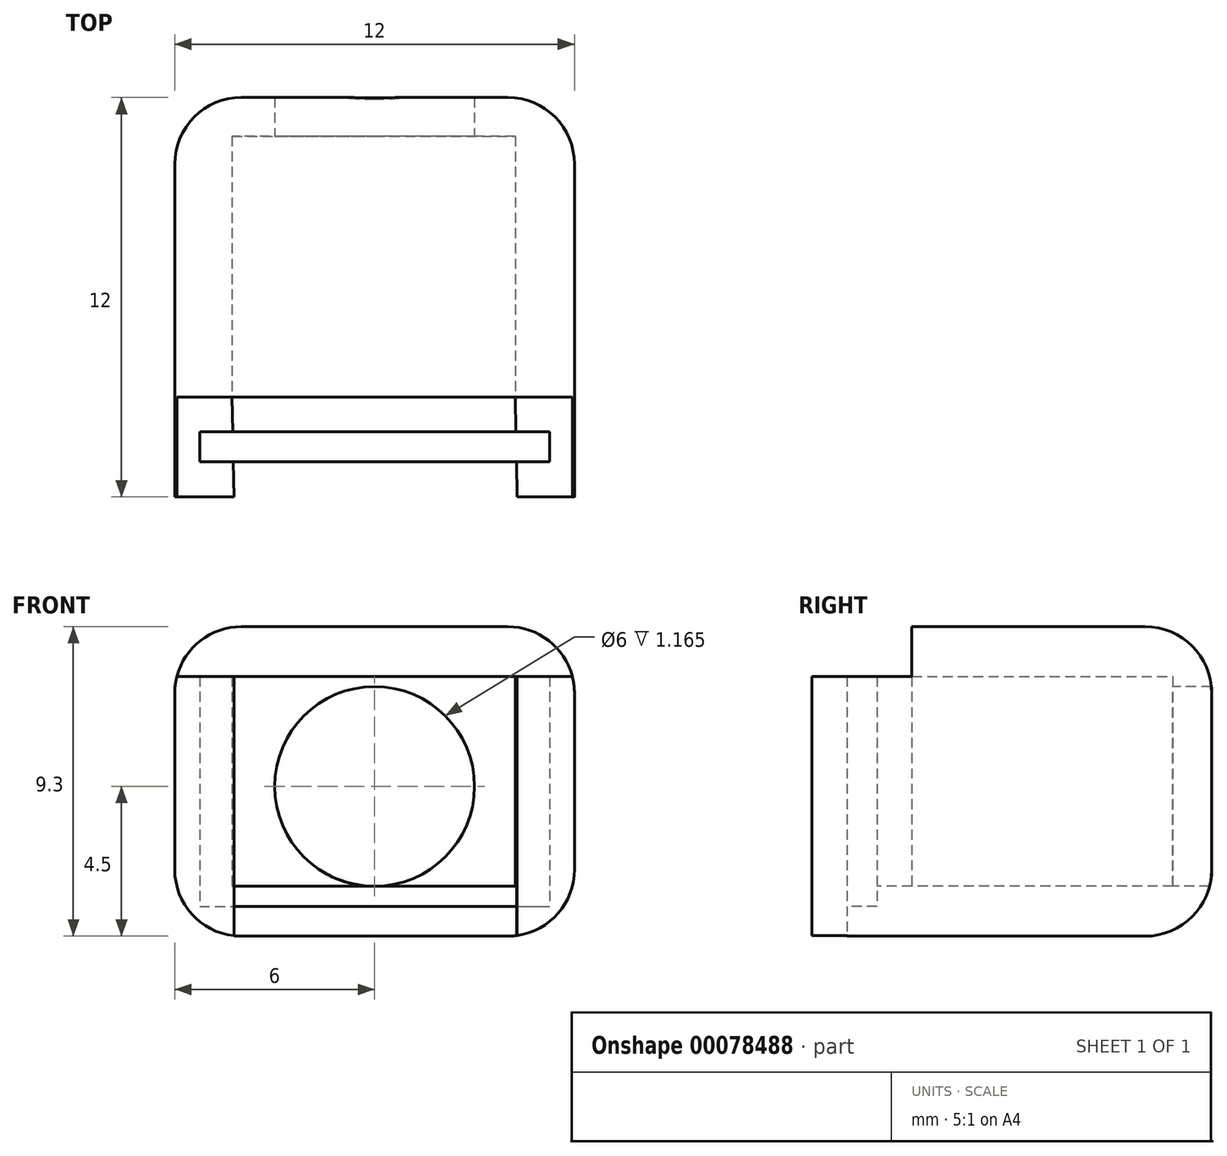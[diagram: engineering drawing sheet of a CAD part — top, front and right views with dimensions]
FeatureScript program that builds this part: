
annotation { "Feature Type Name" : "Feature", "Feature Type Description" : "" }
export const myFeature = defineFeature(function(context is Context, id is Id, definition is map)
    precondition{}
    {
        {
            var Q0;
            Q0=qCreatedBy(makeId("Top.planeOp"),FACE);
            var sketch = newSketch(context, id + "F0", { "sketchPlane" : qUnion([Q0])});
            skPoint(sketch, "E0.rect.middle", {"position": v(0, 0) * mm});
            skLineSegment(sketch, "E1.rect.bottom", {"start": v(-6, -1.5) * mm, "end": v(6, -1.5) * mm});
            skLineSegment(sketch, "E1.rect.top", {"start": v(-6, 1.5) * mm, "end": v(-4.28, 1.5) * mm});
            skLineSegment(sketch, "E1.rect.left", {"start": v(-6, -1.5) * mm, "end": v(-6, 1.5) * mm});
            skLineSegment(sketch, "E1.rect.right", {"start": v(6, -1.5) * mm, "end": v(6, 1.5) * mm});
            skLineSegment(sketch, "E2.rect.bottom", {"start": v(5.25, -0.45) * mm, "end": v(-5.25, -0.45) * mm});
            skLineSegment(sketch, "E2.rect.top", {"start": v(5.25, 0.45) * mm, "end": v(-5.25, 0.45) * mm});
            skLineSegment(sketch, "E2.rect.left", {"start": v(5.25, -0.45) * mm, "end": v(5.25, 0.45) * mm});
            skLineSegment(sketch, "E2.rect.right", {"start": v(-5.25, -0.45) * mm, "end": v(-5.25, 0.45) * mm});
            skLineSegment(sketch, "E3.rect.bottom", {"start": v(-4.22, -1.5) * mm, "end": v(4.28, -1.5) * mm});
            skLineSegment(sketch, "E3.rect.left", {"start": v(-4.22, -1.5) * mm, "end": v(-4.28, 1.5) * mm});
            skLineSegment(sketch, "E3.rect.right", {"start": v(4.28, -1.5) * mm, "end": v(4.22, 1.5) * mm});
            skLineSegment(sketch, "E4.trimOffspring", {"start": v(4.22, 1.5) * mm, "end": v(6, 1.5) * mm});
            skLineSegment(sketch, "E5", {"start": v(-4.28, 1.5) * mm, "end": v(4.22, 1.5) * mm, "construction": true});
            skLineSegment(sketch, "E6.bottom", {"start": v(6, 1.5) * mm, "end": v(-6, 1.5) * mm});
            skLineSegment(sketch, "E7.bottom", {"start": v(4.22, 1.5) * mm, "end": v(-6, 1.5) * mm});
            skLineSegment(sketch, "E8.bottom", {"start": v(-6, 1.5) * mm, "end": v(6, 1.5) * mm});
            skLineSegment(sketch, "E8.top", {"start": v(-6, 10.5) * mm, "end": v(6, 10.5) * mm});
            skLineSegment(sketch, "E8.left", {"start": v(-6, 1.5) * mm, "end": v(-6, 10.5) * mm});
            skLineSegment(sketch, "E8.right", {"start": v(6, 1.5) * mm, "end": v(6, 10.5) * mm});
            skLineSegment(sketch, "E9", {"start": v(-4.28, 1.5) * mm, "end": v(-4.28, 10.5) * mm});
            skLineSegment(sketch, "E10", {"start": v(4.22, 1.5) * mm, "end": v(4.22, 10.5) * mm});
            skLineSegment(sketch, "E11", {"start": v(6, 9.33) * mm, "end": v(-6, 9.33) * mm});
            skSolve(sketch);
        }
        {
            var Q0;
            {var subQ0=sQuery(id+"F0.wireOp",EDGE,"E6.right");Q0=makeQuery(id+"F0.imprint","IMPRINT",FACE,{"disambiguationData":[TD([[makeQuery(id+"F0.imprint","IMPRINT",EDGE,{"derivedFrom":subQ0}),-1.0]])]});}
            var Q1;
            Q1=makeQuery(id+"F0.imprint","IMPRINT",FACE,{"disambiguationData":[TD([[makeQuery(id+"F0.imprint","IMPRINT",EDGE,{"derivedFrom":sQuery(id+"F0.wireOp",EDGE,"E7.bottom")}),-1.0]])]});
            var Q2;
            {var subQ5=sQuery(id+"F0.wireOp",EDGE,"E7.bottom");Q2=makeQuery(id+"F0.imprint","IMPRINT",FACE,{"disambiguationData":[TD([[makeQuery(id+"F0.imprint","IMPRINT",EDGE,{"derivedFrom":subQ5}),1.0]])]});}
            var Q3;
            {var subQ8=sQuery(id+"F0.wireOp",EDGE,"E1.rect.right");Q3=makeQuery(id+"F0.imprint","IMPRINT",FACE,{"disambiguationData":[TD([[makeQuery(id+"F0.imprint","IMPRINT",EDGE,{"derivedFrom":subQ8}),1.0]])]});}
            var Q4;
            {var subQ5=sQuery(id+"F0.wireOp",EDGE,"E3.rect.bottom");Q4=makeQuery(id+"F0.imprint","IMPRINT",FACE,{"disambiguationData":[TD([[makeQuery(id+"F0.imprint","IMPRINT",EDGE,{"derivedFrom":subQ5}),1.0]])]});}
            var Q5;
            {var subQ4=sQuery(id+"F0.wireOp",EDGE,"E1.rect.left");Q5=makeQuery(id+"F0.imprint","IMPRINT",FACE,{"disambiguationData":[TD([[makeQuery(id+"F0.imprint","IMPRINT",EDGE,{"derivedFrom":subQ4}),-1.0]])]});}
            var Q6;
            {var subQ0=sQuery(id+"F0.wireOp",EDGE,"E6.left");Q6=makeQuery(id+"F0.imprint","IMPRINT",FACE,{"disambiguationData":[TD([[makeQuery(id+"F0.imprint","IMPRINT",EDGE,{"derivedFrom":subQ0}),1.0]])]});}
            var Q7;
            {var subQ0=sQuery(id+"F0.wireOp",EDGE,"E3.rect.right");var subQ1=sQuery(id+"F0.wireOp",EDGE,"E2.rect.bottom");var subQ2=makeQuery(id+"F0.imprint","INTERSECT",VERTEX,{"derivedFrom":[subQ1,subQ0]});Q7=makeQuery(id+"F0.imprint","IMPRINT",FACE,{"disambiguationData":[TD([[makeQuery(id+"F0.imprint","IMPRINT",EDGE,{"disambiguationData":[TD([[subQ2,-1.0]])],"derivedFrom":subQ1}),-1.0]])]});}
            var Q8;
            {var subQ0=sQuery(id+"F0.wireOp",EDGE,"E2.rect.right");Q8=makeQuery(id+"F0.imprint","IMPRINT",FACE,{"disambiguationData":[TD([[makeQuery(id+"F0.imprint","IMPRINT",EDGE,{"derivedFrom":subQ0}),-1.0]])]});}
            var Q9;
            {var subQ0=sQuery(id+"F0.wireOp",EDGE,"E2.rect.left");Q9=makeQuery(id+"F0.imprint","IMPRINT",FACE,{"disambiguationData":[TD([[makeQuery(id+"F0.imprint","IMPRINT",EDGE,{"derivedFrom":subQ0}),1.0]])]});}
            var Q10;
            {var subQ0=sQuery(id+"F0.wireOp",EDGE,"E8.left");var subQ5=sQuery(id+"F0.wireOp",EDGE,"E11");var subQ6=makeQuery(id+"F0.imprint","INTERSECT",VERTEX,{"derivedFrom":[subQ0,subQ5]});Q10=makeQuery(id+"F0.imprint","IMPRINT",FACE,{"disambiguationData":[TD([[makeQuery(id+"F0.imprint","IMPRINT",EDGE,{"disambiguationData":[TD([[subQ6,1.0]])],"derivedFrom":subQ5}),1.0]])]});}
            var Q11;
            {var subQ0=sQuery(id+"F0.wireOp",EDGE,"E8.left");var subQ1=sQuery(id+"F0.wireOp",EDGE,"E8.top");var subQ2=makeQuery(id+"F0.imprint","INTERSECT",VERTEX,{"derivedFrom":[subQ1,subQ0]});Q11=makeQuery(id+"F0.imprint","IMPRINT",FACE,{"disambiguationData":[TD([[makeQuery(id+"F0.imprint","IMPRINT",EDGE,{"disambiguationData":[TD([[subQ2,-1.0]])],"derivedFrom":subQ1}),-1.0]])]});}
            var Q12;
            {var subQ0=sQuery(id+"F0.wireOp",EDGE,"E9");var subQ1=sQuery(id+"F0.wireOp",EDGE,"E8.top");var subQ2=makeQuery(id+"F0.imprint","INTERSECT",VERTEX,{"derivedFrom":[subQ1,subQ0]});Q12=makeQuery(id+"F0.imprint","IMPRINT",FACE,{"disambiguationData":[TD([[makeQuery(id+"F0.imprint","IMPRINT",EDGE,{"disambiguationData":[TD([[subQ2,-1.0]])],"derivedFrom":subQ1}),-1.0]])]});}
            var Q13;
            {var subQ0=sQuery(id+"F0.wireOp",EDGE,"E8.right");var subQ1=sQuery(id+"F0.wireOp",EDGE,"E8.top");var subQ2=makeQuery(id+"F0.imprint","INTERSECT",VERTEX,{"derivedFrom":[subQ1,subQ0]});Q13=makeQuery(id+"F0.imprint","IMPRINT",FACE,{"disambiguationData":[TD([[makeQuery(id+"F0.imprint","IMPRINT",EDGE,{"disambiguationData":[TD([[subQ2,1.0]])],"derivedFrom":subQ1}),-1.0]])]});}
            var Q14;
            {var subQ0=sQuery(id+"F0.wireOp",EDGE,"E8.right");var subQ5=sQuery(id+"F0.wireOp",EDGE,"E11");var subQ6=makeQuery(id+"F0.imprint","INTERSECT",VERTEX,{"derivedFrom":[subQ0,subQ5]});Q14=makeQuery(id+"F0.imprint","IMPRINT",FACE,{"disambiguationData":[TD([[makeQuery(id+"F0.imprint","IMPRINT",EDGE,{"disambiguationData":[TD([[subQ6,-1.0]])],"derivedFrom":subQ5}),1.0]])]});}
            var Q15;
            {var subQ0=sQuery(id+"F0.wireOp",EDGE,"E3.rect.right");var subQ1=sQuery(id+"F0.wireOp",EDGE,"E2.rect.top");var subQ2=makeQuery(id+"F0.imprint","INTERSECT",VERTEX,{"derivedFrom":[subQ1,subQ0]});Q15=makeQuery(id+"F0.imprint","IMPRINT",FACE,{"disambiguationData":[TD([[makeQuery(id+"F0.imprint","IMPRINT",EDGE,{"disambiguationData":[TD([[subQ2,-1.0]])],"derivedFrom":subQ1}),-1.0]])]});}
            var Q16;
            {var subQ0=sQuery(id+"F0.wireOp",EDGE,"E9");var subQ5=sQuery(id+"F0.wireOp",EDGE,"E11");var subQ6=makeQuery(id+"F0.imprint","INTERSECT",VERTEX,{"derivedFrom":[subQ0,subQ5]});Q16=makeQuery(id+"F0.imprint","IMPRINT",FACE,{"disambiguationData":[TD([[makeQuery(id+"F0.imprint","IMPRINT",EDGE,{"disambiguationData":[TD([[subQ6,1.0]])],"derivedFrom":subQ5}),1.0]])]});}
            extrude(context, id + "F1", {"entities" : qUnion([Q0, Q1, Q2, Q3, Q4, Q5, Q6, Q7, Q8, Q9, Q10, Q11, Q12, Q13, Q14, Q15, Q16]), "depth" : 0.9 * mm});
        }
        {
            var Q0;
            {var subQ0=sQuery(id+"F0.wireOp",EDGE,"E6.left");Q0=makeQuery(id+"F0.imprint","IMPRINT",FACE,{"disambiguationData":[TD([[makeQuery(id+"F0.imprint","IMPRINT",EDGE,{"derivedFrom":subQ0}),1.0]])]});}
            var Q1;
            {var subQ0=sQuery(id+"F0.wireOp",EDGE,"E6.right");Q1=makeQuery(id+"F0.imprint","IMPRINT",FACE,{"disambiguationData":[TD([[makeQuery(id+"F0.imprint","IMPRINT",EDGE,{"derivedFrom":subQ0}),-1.0]])]});}
            var Q2;
            {var subQ5=sQuery(id+"F0.wireOp",EDGE,"E3.rect.bottom");Q2=makeQuery(id+"F0.imprint","IMPRINT",FACE,{"disambiguationData":[TD([[makeQuery(id+"F0.imprint","IMPRINT",EDGE,{"derivedFrom":subQ5}),1.0]])]});}
            var Q3;
            {var subQ4=sQuery(id+"F0.wireOp",EDGE,"E1.rect.left");Q3=makeQuery(id+"F0.imprint","IMPRINT",FACE,{"disambiguationData":[TD([[makeQuery(id+"F0.imprint","IMPRINT",EDGE,{"derivedFrom":subQ4}),-1.0]])]});}
            var Q4;
            {var subQ8=sQuery(id+"F0.wireOp",EDGE,"E1.rect.right");Q4=makeQuery(id+"F0.imprint","IMPRINT",FACE,{"disambiguationData":[TD([[makeQuery(id+"F0.imprint","IMPRINT",EDGE,{"derivedFrom":subQ8}),1.0]])]});}
            var Q5;
            {var subQ5=sQuery(id+"F0.wireOp",EDGE,"E7.bottom");Q5=makeQuery(id+"F0.imprint","IMPRINT",FACE,{"disambiguationData":[TD([[makeQuery(id+"F0.imprint","IMPRINT",EDGE,{"derivedFrom":subQ5}),1.0]])]});}
            var Q6;
            {var subQ0=sQuery(id+"F0.wireOp",EDGE,"E8.right");var subQ5=sQuery(id+"F0.wireOp",EDGE,"E11");var subQ6=makeQuery(id+"F0.imprint","INTERSECT",VERTEX,{"derivedFrom":[subQ0,subQ5]});Q6=makeQuery(id+"F0.imprint","IMPRINT",FACE,{"disambiguationData":[TD([[makeQuery(id+"F0.imprint","IMPRINT",EDGE,{"disambiguationData":[TD([[subQ6,-1.0]])],"derivedFrom":subQ5}),1.0]])]});}
            var Q7;
            {var subQ0=sQuery(id+"F0.wireOp",EDGE,"E3.rect.right");var subQ1=sQuery(id+"F0.wireOp",EDGE,"E2.rect.top");var subQ2=makeQuery(id+"F0.imprint","INTERSECT",VERTEX,{"derivedFrom":[subQ1,subQ0]});Q7=makeQuery(id+"F0.imprint","IMPRINT",FACE,{"disambiguationData":[TD([[makeQuery(id+"F0.imprint","IMPRINT",EDGE,{"disambiguationData":[TD([[subQ2,-1.0]])],"derivedFrom":subQ1}),-1.0]])]});}
            var Q8;
            {var subQ0=sQuery(id+"F0.wireOp",EDGE,"E9");var subQ5=sQuery(id+"F0.wireOp",EDGE,"E11");var subQ6=makeQuery(id+"F0.imprint","INTERSECT",VERTEX,{"derivedFrom":[subQ0,subQ5]});Q8=makeQuery(id+"F0.imprint","IMPRINT",FACE,{"disambiguationData":[TD([[makeQuery(id+"F0.imprint","IMPRINT",EDGE,{"disambiguationData":[TD([[subQ6,1.0]])],"derivedFrom":subQ5}),1.0]])]});}
            var Q9;
            {var subQ0=sQuery(id+"F0.wireOp",EDGE,"E8.left");var subQ5=sQuery(id+"F0.wireOp",EDGE,"E11");var subQ6=makeQuery(id+"F0.imprint","INTERSECT",VERTEX,{"derivedFrom":[subQ0,subQ5]});Q9=makeQuery(id+"F0.imprint","IMPRINT",FACE,{"disambiguationData":[TD([[makeQuery(id+"F0.imprint","IMPRINT",EDGE,{"disambiguationData":[TD([[subQ6,1.0]])],"derivedFrom":subQ5}),1.0]])]});}
            var Q10;
            {var subQ0=sQuery(id+"F0.wireOp",EDGE,"E8.left");var subQ1=sQuery(id+"F0.wireOp",EDGE,"E8.top");var subQ2=makeQuery(id+"F0.imprint","INTERSECT",VERTEX,{"derivedFrom":[subQ1,subQ0]});Q10=makeQuery(id+"F0.imprint","IMPRINT",FACE,{"disambiguationData":[TD([[makeQuery(id+"F0.imprint","IMPRINT",EDGE,{"disambiguationData":[TD([[subQ2,-1.0]])],"derivedFrom":subQ1}),-1.0]])]});}
            var Q11;
            {var subQ0=sQuery(id+"F0.wireOp",EDGE,"E9");var subQ1=sQuery(id+"F0.wireOp",EDGE,"E8.top");var subQ2=makeQuery(id+"F0.imprint","INTERSECT",VERTEX,{"derivedFrom":[subQ1,subQ0]});Q11=makeQuery(id+"F0.imprint","IMPRINT",FACE,{"disambiguationData":[TD([[makeQuery(id+"F0.imprint","IMPRINT",EDGE,{"disambiguationData":[TD([[subQ2,-1.0]])],"derivedFrom":subQ1}),-1.0]])]});}
            var Q12;
            {var subQ0=sQuery(id+"F0.wireOp",EDGE,"E8.right");var subQ1=sQuery(id+"F0.wireOp",EDGE,"E8.top");var subQ2=makeQuery(id+"F0.imprint","INTERSECT",VERTEX,{"derivedFrom":[subQ1,subQ0]});Q12=makeQuery(id+"F0.imprint","IMPRINT",FACE,{"disambiguationData":[TD([[makeQuery(id+"F0.imprint","IMPRINT",EDGE,{"disambiguationData":[TD([[subQ2,1.0]])],"derivedFrom":subQ1}),-1.0]])]});}
            extrude(context, id + "F2", {"entities" : qUnion([Q0, Q1, Q2, Q3, Q4, Q5, Q6, Q7, Q8, Q9, Q10, Q11, Q12]), "operationType" : NewBodyOperationType.ADD, "depth" : 1.5 * mm});
        }
        {
            var Q0;
            {var subQ9=sQuery(id+"F0.wireOp",EDGE,"E1.rect.top");Q0=makeQuery(id+"F0.imprint","IMPRINT",FACE,{"disambiguationData":[TD([[makeQuery(id+"F0.imprint","IMPRINT",EDGE,{"derivedFrom":subQ9}),-1.0]])]});}
            var Q1;
            {var subQ4=sQuery(id+"F0.wireOp",EDGE,"E1.rect.right");Q1=makeQuery(id+"F0.imprint","IMPRINT",FACE,{"disambiguationData":[TD([[makeQuery(id+"F0.imprint","IMPRINT",EDGE,{"derivedFrom":subQ4}),1.0]])]});}
            var Q2;
            {var subQ4=sQuery(id+"F0.wireOp",EDGE,"E1.rect.left");Q2=makeQuery(id+"F0.imprint","IMPRINT",FACE,{"disambiguationData":[TD([[makeQuery(id+"F0.imprint","IMPRINT",EDGE,{"derivedFrom":subQ4}),-1.0]])]});}
            var Q3;
            {var subQ0=sQuery(id+"F0.wireOp",EDGE,"E6.right");Q3=makeQuery(id+"F0.imprint","IMPRINT",FACE,{"disambiguationData":[TD([[makeQuery(id+"F0.imprint","IMPRINT",EDGE,{"derivedFrom":subQ0}),-1.0]])]});}
            var Q4;
            {var subQ0=sQuery(id+"F0.wireOp",EDGE,"E6.left");Q4=makeQuery(id+"F0.imprint","IMPRINT",FACE,{"disambiguationData":[TD([[makeQuery(id+"F0.imprint","IMPRINT",EDGE,{"derivedFrom":subQ0}),1.0]])]});}
            var Q5;
            {var subQ0=sQuery(id+"F0.wireOp",EDGE,"E8.left");var subQ5=sQuery(id+"F0.wireOp",EDGE,"E11");var subQ6=makeQuery(id+"F0.imprint","INTERSECT",VERTEX,{"derivedFrom":[subQ0,subQ5]});Q5=makeQuery(id+"F0.imprint","IMPRINT",FACE,{"disambiguationData":[TD([[makeQuery(id+"F0.imprint","IMPRINT",EDGE,{"disambiguationData":[TD([[subQ6,1.0]])],"derivedFrom":subQ5}),1.0]])]});}
            var Q6;
            {var subQ0=sQuery(id+"F0.wireOp",EDGE,"E8.right");var subQ5=sQuery(id+"F0.wireOp",EDGE,"E11");var subQ6=makeQuery(id+"F0.imprint","INTERSECT",VERTEX,{"derivedFrom":[subQ0,subQ5]});Q6=makeQuery(id+"F0.imprint","IMPRINT",FACE,{"disambiguationData":[TD([[makeQuery(id+"F0.imprint","IMPRINT",EDGE,{"disambiguationData":[TD([[subQ6,-1.0]])],"derivedFrom":subQ5}),1.0]])]});}
            var Q7;
            {var subQ0=sQuery(id+"F0.wireOp",EDGE,"E8.left");var subQ1=sQuery(id+"F0.wireOp",EDGE,"E8.top");var subQ2=makeQuery(id+"F0.imprint","INTERSECT",VERTEX,{"derivedFrom":[subQ1,subQ0]});Q7=makeQuery(id+"F0.imprint","IMPRINT",FACE,{"disambiguationData":[TD([[makeQuery(id+"F0.imprint","IMPRINT",EDGE,{"disambiguationData":[TD([[subQ2,-1.0]])],"derivedFrom":subQ1}),-1.0]])]});}
            var Q8;
            {var subQ0=sQuery(id+"F0.wireOp",EDGE,"E9");var subQ1=sQuery(id+"F0.wireOp",EDGE,"E8.top");var subQ2=makeQuery(id+"F0.imprint","INTERSECT",VERTEX,{"derivedFrom":[subQ1,subQ0]});Q8=makeQuery(id+"F0.imprint","IMPRINT",FACE,{"disambiguationData":[TD([[makeQuery(id+"F0.imprint","IMPRINT",EDGE,{"disambiguationData":[TD([[subQ2,-1.0]])],"derivedFrom":subQ1}),-1.0]])]});}
            var Q9;
            {var subQ0=sQuery(id+"F0.wireOp",EDGE,"E8.right");var subQ1=sQuery(id+"F0.wireOp",EDGE,"E8.top");var subQ2=makeQuery(id+"F0.imprint","INTERSECT",VERTEX,{"derivedFrom":[subQ1,subQ0]});Q9=makeQuery(id+"F0.imprint","IMPRINT",FACE,{"disambiguationData":[TD([[makeQuery(id+"F0.imprint","IMPRINT",EDGE,{"disambiguationData":[TD([[subQ2,1.0]])],"derivedFrom":subQ1}),-1.0]])]});}
            extrude(context, id + "F3", {"entities" : qUnion([Q0, Q1, Q2, Q3, Q4, Q5, Q6, Q7, Q8, Q9]), "operationType" : NewBodyOperationType.ADD, "depth" : 7.8 * mm});
        }
        {
            var Q0;
            Q0=makeQuery(id+"F3.opExtrude","CAP_FACE",FACE,{"disambiguationData":[OSD([sQuery(id+"F0.wireOp",EDGE,"E1.rect.bottom"),sQuery(id+"F0.wireOp",EDGE,"E1.rect.left"),sQuery(id+"F0.wireOp",EDGE,"E1.rect.right"),sQuery(id+"F0.wireOp",EDGE,"E2.rect.bottom"),sQuery(id+"F0.wireOp",EDGE,"E2.rect.top"),sQuery(id+"F0.wireOp",EDGE,"E2.rect.left"),sQuery(id+"F0.wireOp",EDGE,"E2.rect.right"),sQuery(id+"F0.wireOp",EDGE,"E3.rect.left"),sQuery(id+"F0.wireOp",EDGE,"E3.rect.right"),sQuery(id+"F0.wireOp",EDGE,"E8.top"),sQuery(id+"F0.wireOp",EDGE,"E8.left"),sQuery(id+"F0.wireOp",EDGE,"E8.right"),sQuery(id+"F0.wireOp",EDGE,"E9"),sQuery(id+"F0.wireOp",EDGE,"E10"),sQuery(id+"F0.wireOp",EDGE,"E11")])],"isStart":false});
            cPlane(context, id + "F4", {"entities" : qUnion([Q0]), "cplaneType" : CPlaneType.OFFSET, "offset" : 0 * mm, "width" : 150 * mm, "height" : 150 * mm});
        }
        {
            var Q0;
            Q0=qCreatedBy(id+"F4.planeOp",FACE);
            var sketch = newSketch(context, id + "F5", { "sketchPlane" : qUnion([Q0])});
            skLineSegment(sketch, "E12.bottom", {"start": v(6, 1.5) * mm, "end": v(-6, 1.5) * mm});
            skLineSegment(sketch, "E12.top", {"start": v(6, -1.5) * mm, "end": v(-6, -1.5) * mm});
            skLineSegment(sketch, "E12.left", {"start": v(6, 1.5) * mm, "end": v(6, -1.5) * mm});
            skLineSegment(sketch, "E12.right", {"start": v(-6, 1.5) * mm, "end": v(-6, -1.5) * mm});
            skPoint(sketch, "E12.middle", {"position": v(0, 0) * mm});
            skLineSegment(sketch, "E13.top", {"start": v(6, 10.5) * mm, "end": v(-6, 10.5) * mm});
            skLineSegment(sketch, "E13.left", {"start": v(6, 1.5) * mm, "end": v(6, 10.5) * mm});
            skLineSegment(sketch, "E13.right", {"start": v(-6, 1.5) * mm, "end": v(-6, 10.5) * mm});
            skSolve(sketch);
        }
        {
            var Q0;
            Q0=makeQuery(id+"F5.imprint","IMPRINT",FACE,{"disambiguationData":[TD([[makeQuery(id+"F5.imprint","IMPRINT",EDGE,{"derivedFrom":sQuery(id+"F5.wireOp",EDGE,"E12.bottom")}),-1.0]])]});
            extrude(context, id + "F6", {"entities" : qUnion([Q0]), "operationType" : NewBodyOperationType.ADD, "depth" : 1.5 * mm});
        }
        {
            var Q0;
            Q0=qCreatedBy(makeId("Front.planeOp"),FACE);
            var sketch = newSketch(context, id + "F7", { "sketchPlane" : qUnion([Q0])});
            skLineSegment(sketch, "E14", {"start": v(0, 0) * mm, "end": v(0, 9) * mm, "construction": true});
            skCircle(sketch, "E15", {"center": v(0, 4.5) * mm, "radius": 3 * mm});
            skSolve(sketch);
        }
        {
            var Q0;
            Q0 = qSketchRegion(id + "F7", true);
            extrude(context, id + "F8", {"entities" : qUnion([Q0]), "operationType" : NewBodyOperationType.REMOVE, "endBound" : BoundingType.THROUGH_ALL, "oppositeDirection" : true, "depth" : 25 * mm});
        }
        {
            var Q0;
            {var subQ0=sQuery(id+"F0.wireOp",EDGE,"E8.right");var subQ1=sQuery(id+"F0.wireOp",EDGE,"E8.top");Q0=makeQuery(id+"F6.boolean.opBoolean","MERGE",EDGE,{"derivedFrom":[makeQuery(id+"F3.boolean.opBoolean","MERGE",EDGE,{"derivedFrom":[makeQuery(id+"F2.boolean.opBoolean","MERGE",EDGE,{"derivedFrom":[makeQuery(id+"F1.opExtrude","SWEPT_EDGE",EDGE,{"disambiguationData":[OSD([subQ1,subQ0])]}),makeQuery(id+"F2.opExtrude","SWEPT_EDGE",EDGE,{"disambiguationData":[OSD([subQ1,subQ0])]})]}),makeQuery(id+"F3.opExtrude","SWEPT_EDGE",EDGE,{"disambiguationData":[OSD([subQ1,subQ0])]})]}),makeQuery(id+"F6.opExtrude","SWEPT_EDGE",EDGE,{"disambiguationData":[OSD([sQuery(id+"F5.wireOp",EDGE,"E13.top"),sQuery(id+"F5.wireOp",EDGE,"E13.left")])]})]});}
            var Q1;
            Q1=makeQuery(id+"F6.opExtrude","CAP_EDGE",EDGE,{"disambiguationData":[OSD([sQuery(id+"F5.wireOp",EDGE,"E13.top")])],"isStart":false});
            var Q2;
            Q2=makeQuery(id+"F6.opExtrude","CAP_EDGE",EDGE,{"disambiguationData":[OSD([sQuery(id+"F5.wireOp",EDGE,"E13.left")])],"isStart":false});
            var Q3;
            Q3=makeQuery(id+"F1.opExtrude","CAP_EDGE",EDGE,{"disambiguationData":[OSD([sQuery(id+"F0.wireOp",EDGE,"E1.rect.right"),sQuery(id+"F0.wireOp",EDGE,"E8.right")])],"isStart":true});
            var Q4;
            Q4=makeQuery(id+"F1.opExtrude","CAP_EDGE",EDGE,{"disambiguationData":[OSD([sQuery(id+"F0.wireOp",EDGE,"E8.top")])],"isStart":true});
            var Q5;
            Q5=makeQuery(id+"F1.opExtrude","CAP_EDGE",EDGE,{"disambiguationData":[OSD([sQuery(id+"F0.wireOp",EDGE,"E1.rect.left"),sQuery(id+"F0.wireOp",EDGE,"E8.left")])],"isStart":true});
            var Q6;
            {var subQ0=sQuery(id+"F0.wireOp",EDGE,"E8.left");var subQ1=sQuery(id+"F0.wireOp",EDGE,"E8.top");Q6=makeQuery(id+"F6.boolean.opBoolean","MERGE",EDGE,{"derivedFrom":[makeQuery(id+"F3.boolean.opBoolean","MERGE",EDGE,{"derivedFrom":[makeQuery(id+"F2.boolean.opBoolean","MERGE",EDGE,{"derivedFrom":[makeQuery(id+"F1.opExtrude","SWEPT_EDGE",EDGE,{"disambiguationData":[OSD([subQ1,subQ0])]}),makeQuery(id+"F2.opExtrude","SWEPT_EDGE",EDGE,{"disambiguationData":[OSD([subQ1,subQ0])]})]}),makeQuery(id+"F3.opExtrude","SWEPT_EDGE",EDGE,{"disambiguationData":[OSD([subQ1,subQ0])]})]}),makeQuery(id+"F6.opExtrude","SWEPT_EDGE",EDGE,{"disambiguationData":[OSD([sQuery(id+"F5.wireOp",EDGE,"E13.top"),sQuery(id+"F5.wireOp",EDGE,"E13.right")])]})]});}
            var Q7;
            Q7=makeQuery(id+"F6.opExtrude","CAP_EDGE",EDGE,{"disambiguationData":[OSD([sQuery(id+"F5.wireOp",EDGE,"E13.right")])],"isStart":false});
            fillet(context, id + "F9", {"entities" : qUnion([Q0, Q1, Q2, Q3, Q4, Q5, Q6, Q7]), "radius" : 2 * mm, "tangentPropagation" : true, "allowEdgeOverflow" : false});
        }
    });
